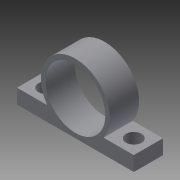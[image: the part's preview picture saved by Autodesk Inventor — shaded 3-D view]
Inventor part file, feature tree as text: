
AUTODESK INVENTOR PART (.ipt)
format: ipt  version: 2013 (Build 170138000, 138)  size: 129,536 bytes
history: native  units: in
note: dims shown in document units (in); Inventor stores cm internally (conversion verified against a paired STEP export)
features: sketch x2, other x2, sheet_metal_op x1
ambient origin geometry x8: Origin, YZ Plane, XZ Plane, XY Plane, X Axis, Y Axis, Z Axis, Center Point
bodies: Solid1 (feature_tree)
feature tree (5):
  sheet_metal_op  "Face1"
  sketch  "Sketch1"  dims[d0=2.0in]
  other  "Plate1"
  sketch  "Sketch2"  dims[d1=1.1811in d2=1.0236in d3=0.25in d4=0.25in d5=1.0in d6=0.5in d7=0.266in d8=0.266in d9=0.25in d10=0.25in d12=0.25in d13=0.25in d14=0.5in d15=0.0in]
  other  "Cut1"
